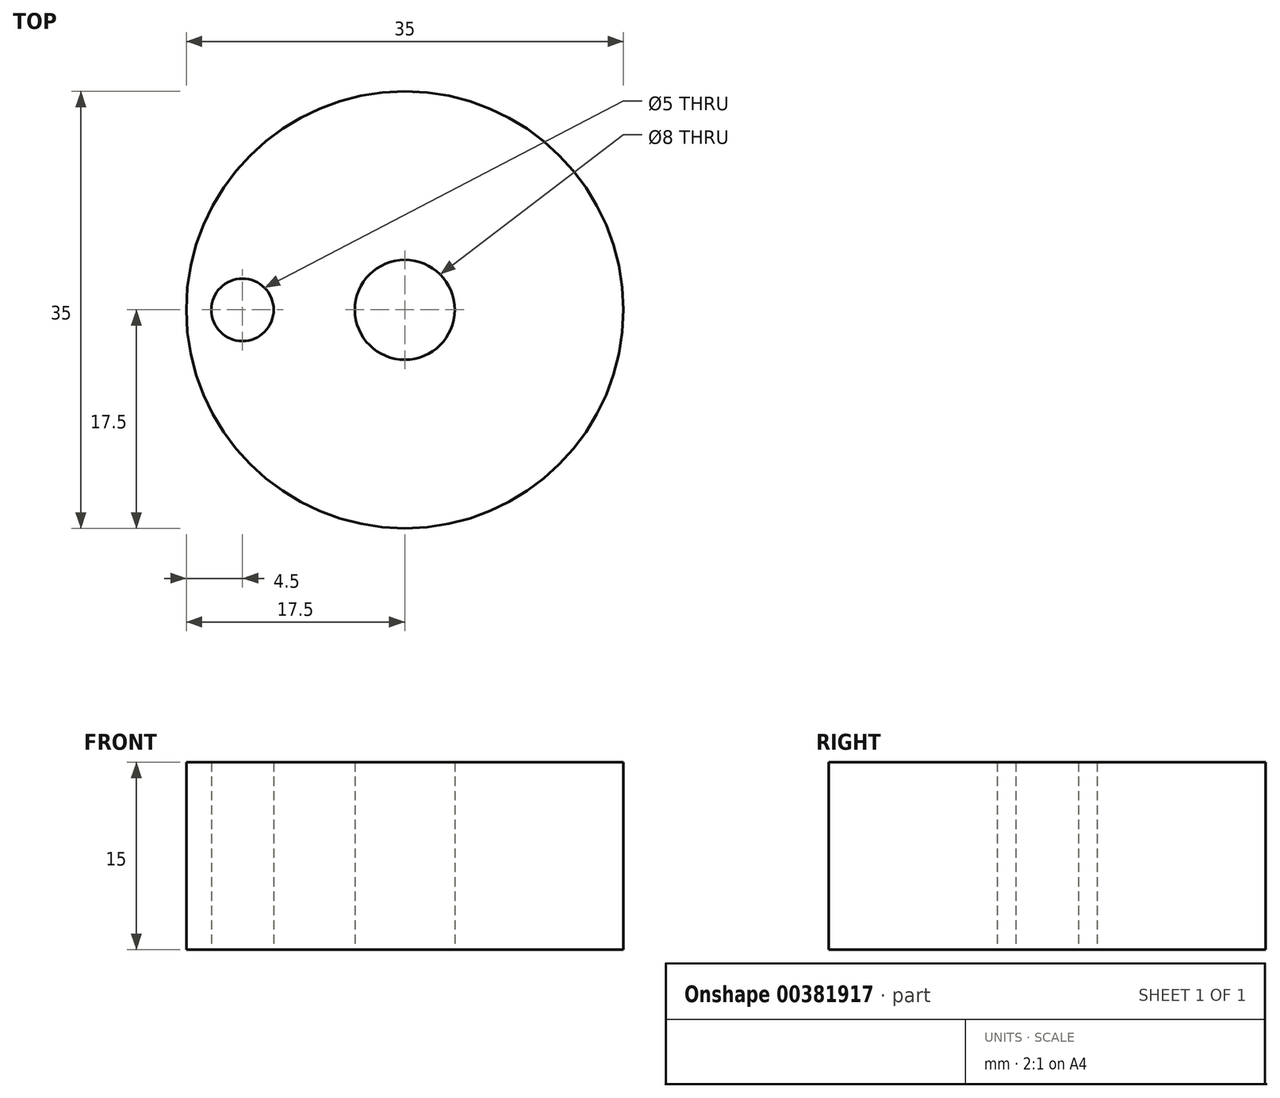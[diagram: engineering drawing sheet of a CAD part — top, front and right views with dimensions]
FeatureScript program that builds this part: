
annotation { "Feature Type Name" : "Feature", "Feature Type Description" : "" }
export const myFeature = defineFeature(function(context is Context, id is Id, definition is map)
    precondition{}
    {
        {
            var Q0;
            Q0=qCreatedBy(makeId("Top.planeOp"),FACE);
            var sketch = newSketch(context, id + "F0", { "sketchPlane" : qUnion([Q0])});
            skLineSegment(sketch, "E0.bottom", {"start": v(0, 0) * mm, "end": v(160, 0) * mm, "construction": true});
            skLineSegment(sketch, "E0.top", {"start": v(0, 80) * mm, "end": v(160, 80) * mm, "construction": true});
            skLineSegment(sketch, "E0.left", {"start": v(0, 0) * mm, "end": v(0, 80) * mm, "construction": true});
            skLineSegment(sketch, "E0.right", {"start": v(160, 0) * mm, "end": v(160, 80) * mm, "construction": true});
            skArc(sketch, "E1", {"start": v(15, 20) * mm, "mid": v(10, 15) * mm, "end": v(15, 10) * mm, "construction": true});
            skLineSegment(sketch, "E2", {"start": v(0, 15) * mm, "end": v(160, 15) * mm, "construction": true});
            skArc(sketch, "E3", {"start": v(145, 10) * mm, "mid": v(150, 15) * mm, "end": v(145, 20) * mm, "construction": true});
            skLineSegment(sketch, "E4", {"start": v(15, 20) * mm, "end": v(145, 20) * mm, "construction": true});
            skLineSegment(sketch, "E5", {"start": v(145, 10) * mm, "end": v(15, 10) * mm, "construction": true});
            skCircle(sketch, "E6", {"center": v(130, 50) * mm, "radius": 4 * mm});
            skCircle(sketch, "E7", {"center": v(130, 50) * mm, "radius": 17.5 * mm});
            skCircle(sketch, "E8", {"center": v(117, 50) * mm, "radius": 2.5 * mm});
            skArc(sketch, "E9", {"start": v(20, 55) * mm, "mid": v(15, 50) * mm, "end": v(20, 45) * mm, "construction": true});
            skArc(sketch, "E10", {"start": v(46, 45) * mm, "mid": v(51, 50) * mm, "end": v(46, 55) * mm, "construction": true});
            skLineSegment(sketch, "E11", {"start": v(20, 50) * mm, "end": v(46, 50) * mm, "construction": true});
            skLineSegment(sketch, "E12", {"start": v(20, 55) * mm, "end": v(46, 55) * mm, "construction": true});
            skLineSegment(sketch, "E13", {"start": v(20, 45) * mm, "end": v(46, 45) * mm, "construction": true});
            skLineSegment(sketch, "E14.bottom", {"start": v(0, 0) * mm, "end": v(30, 0) * mm});
            skLineSegment(sketch, "E14.top", {"start": v(0, 32.5) * mm, "end": v(30, 32.5) * mm});
            skLineSegment(sketch, "E14.left", {"start": v(0, 0) * mm, "end": v(0, 32.5) * mm});
            skLineSegment(sketch, "E14.right", {"start": v(30, 0) * mm, "end": v(30, 32.5) * mm});
            skCircle(sketch, "E15", {"center": v(15, 15) * mm, "radius": 5 * mm});
            skLineSegment(sketch, "E16", {"start": v(30, 32.5) * mm, "end": v(160, 32.5) * mm});
            skLineSegment(sketch, "E17", {"start": v(160, 32.5) * mm, "end": v(160, 22.5) * mm});
            skLineSegment(sketch, "E18", {"start": v(160, 22.5) * mm, "end": v(30, 22.5) * mm});
            skSolve(sketch);
        }
        {
            var Q0;
            Q0=makeQuery(id+"F0.imprint","IMPRINT",FACE,{"disambiguationData":[TD([[makeQuery(id+"F0.imprint","IMPRINT",EDGE,{"derivedFrom":sQuery(id+"F0.wireOp",EDGE,"E6")}),-1.0]])]});
            var Q1;
            Q1=sQuery(id+"F0.wireOp",EDGE,"E8");
            extrude(context, id + "F1", {"entities" : qUnion([Q0]), "surfaceEntities" : qUnion([Q1]), "depth" : (15) * mm});
        }
    });
